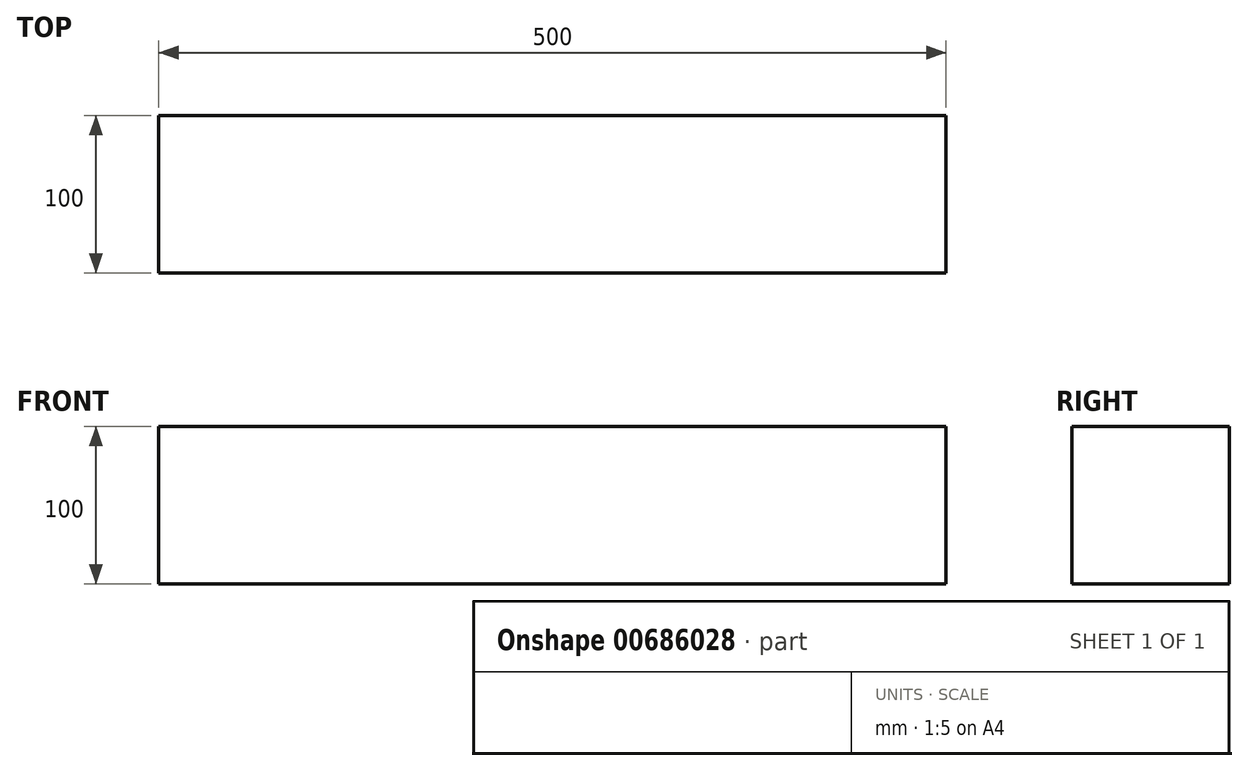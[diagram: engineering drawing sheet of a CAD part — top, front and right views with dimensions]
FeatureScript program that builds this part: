
annotation { "Feature Type Name" : "Feature", "Feature Type Description" : "" }
export const myFeature = defineFeature(function(context is Context, id is Id, definition is map)
    precondition{}
    {
        {
            var Q0;
            Q0=qCreatedBy(makeId("Right.planeOp"),FACE);
            var sketch = newSketch(context, id + "F0", { "sketchPlane" : qUnion([Q0])});
            skLineSegment(sketch, "E0.bottom", {"start": v(50, -50) * mm, "end": v(-50, -50) * mm});
            skLineSegment(sketch, "E0.top", {"start": v(50, 50) * mm, "end": v(-50, 50) * mm});
            skLineSegment(sketch, "E0.left", {"start": v(50, -50) * mm, "end": v(50, 50) * mm});
            skLineSegment(sketch, "E0.right", {"start": v(-50, -50) * mm, "end": v(-50, 50) * mm});
            skPoint(sketch, "E0.middle", {"position": v(0, 0) * mm});
            skSolve(sketch);
        }
        {
            var Q0;
            Q0 = qSketchRegion(id + "F0", true);
            extrude(context, id + "F1", {"entities" : qUnion([Q0]), "depth" : 500 * mm, "offsetDistance" : 25 * mm});
        }
    });
